# Revit family: Keilhauer-Symm-Backless_Bench-Magic_Angled
name_source: partatom
category: Furniture
units: mm (PartAtom-declared; Revit-internal decimal feet)

## family parameters
Always vertical = Yes
Cut with Voids When Loaded = No
OmniClass Number = 23.40.20.00
OmniClass Title = General Furniture and Specialties
Room Calculation Point = No
Shared = No
Work Plane-Based = No

## types (3) — shared parameters
Assembly Code = E2020200
Default Elevation = 0"
Depth = 21 3/4"
Height = 16 1/2"
Keynote = 12500
Low Emitting Finish = Yes
Low Emitting Material = Yes
Manufacturer = Keilhauer
Product Documentation Link = https://keilhauer.com
Revit Model Built By = https://servex-us.com
Salvage or Reuse = Yes
Type Comments = Symm
URL = https://keilhauer.com
Width = 70"
zero-valued in all types: Percentage of Recycled Content

## per-type parameters (varying)
| type | Description |
| 93300 | Backless magic angled bench with 4-leg aluminum base |
| 93301 | Backless magic angled bench with 4-leg ash base |
| 93302 | Backless magic angled bench with 4-leg walnut base |

note: column(s) folded — value = type name in every type: Model

## geometry (parser evidence)
native form markers: Sweep x2
no freeform markers — native parametric forms only
